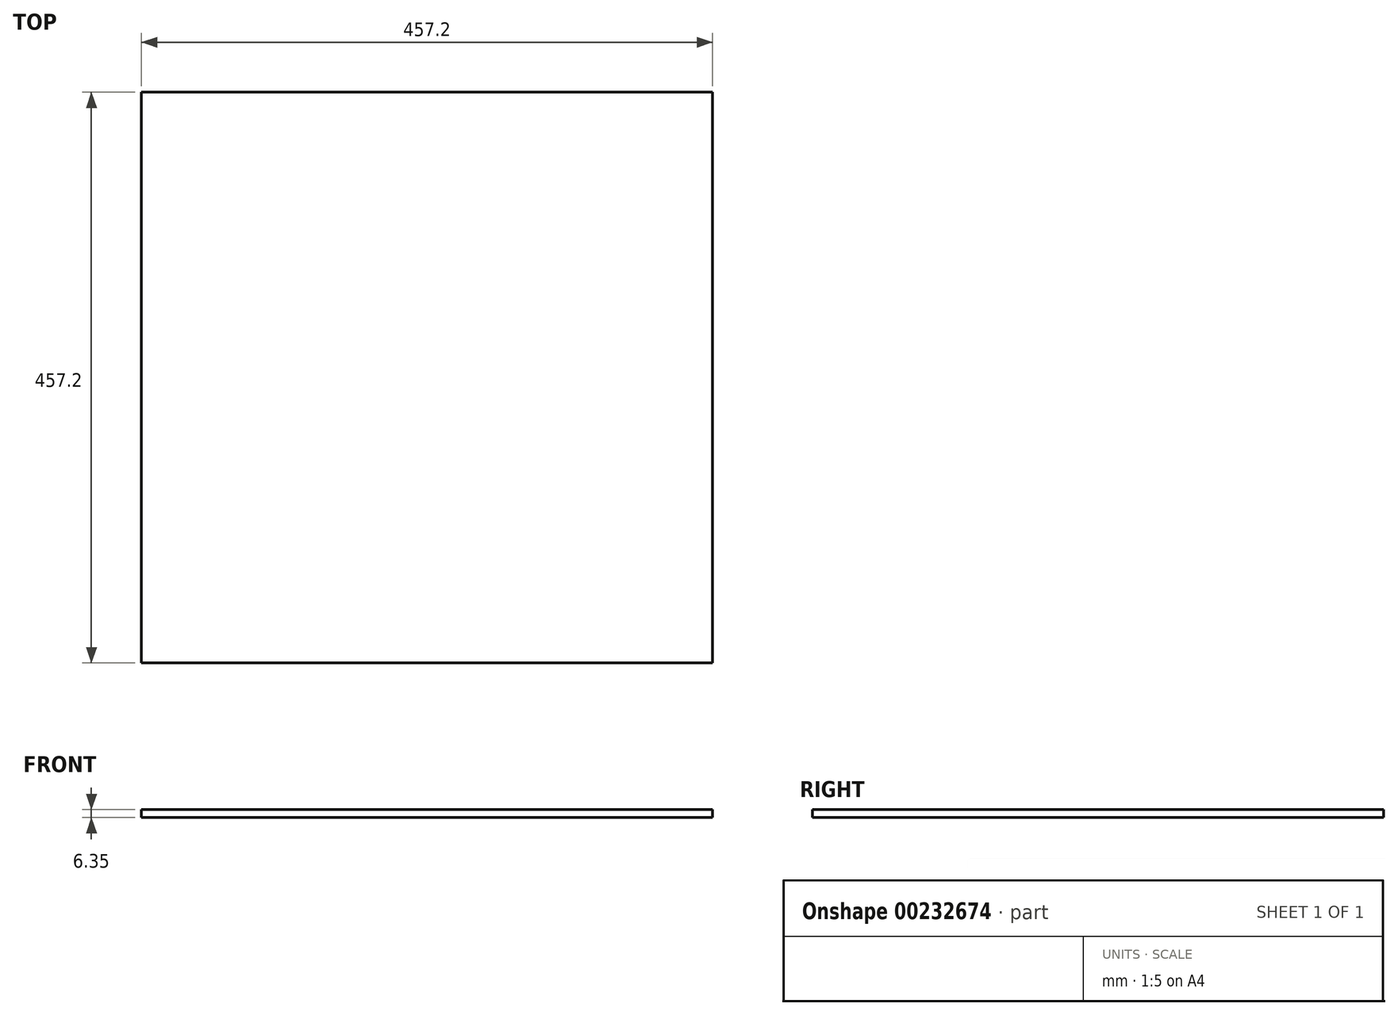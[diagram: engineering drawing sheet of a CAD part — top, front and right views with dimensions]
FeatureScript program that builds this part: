
annotation { "Feature Type Name" : "Feature", "Feature Type Description" : "" }
export const myFeature = defineFeature(function(context is Context, id is Id, definition is map)
    precondition{}
    {
        {
            var Q0;
            Q0=qCreatedBy(makeId("Top.planeOp"),FACE);
            var sketch = newSketch(context, id + "F0", { "sketchPlane" : qUnion([Q0])});
            skLineSegment(sketch, "E0.bottom", {"start": v(-228.6, 228.6) * mm, "end": v(228.6, 228.6) * mm});
            skLineSegment(sketch, "E0.top", {"start": v(-228.6, -228.6) * mm, "end": v(228.6, -228.6) * mm});
            skLineSegment(sketch, "E0.left", {"start": v(-228.6, 228.6) * mm, "end": v(-228.6, -228.6) * mm});
            skLineSegment(sketch, "E0.right", {"start": v(228.6, 228.6) * mm, "end": v(228.6, -228.6) * mm});
            skPoint(sketch, "E0.middle", {"position": v(0, 0) * mm});
            skSolve(sketch);
        }
        {
            var Q0;
            Q0 = qSketchRegion(id + "F0", true);
            extrude(context, id + "F1", {"entities" : qUnion([Q0]), "depth" : 6.35 * mm});
        }
    });
